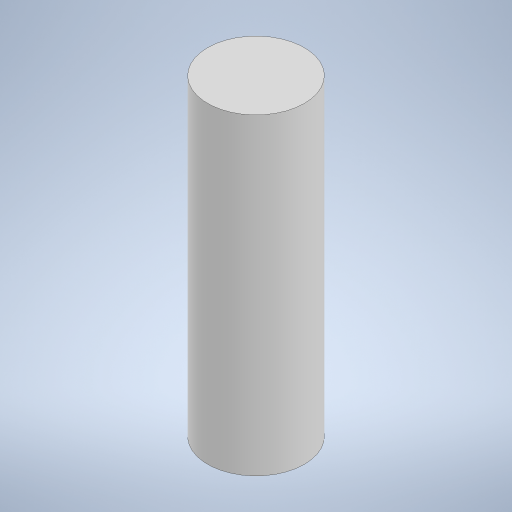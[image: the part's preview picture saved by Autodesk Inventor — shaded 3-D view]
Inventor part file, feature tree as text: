
AUTODESK INVENTOR PART (.ipt)
format: ipt  version: 2023.1 (Build 271208000, 208)  size: 209,408 bytes
history: native  units: mm
features: extrude x1, sketch x1
ambient origin geometry x8: Origin, YZ Plane, XZ Plane, XY Plane, X Axis, Y Axis, Z Axis, Center Point
bodies: Solid1 (feature_tree)
feature tree (2):
  extrude  "Extrusion1"  Depth=9.7mm TaperAngle=0.0deg
  sketch  "Sketch1"  dims[d0=3.0mm d1=9.7mm d2=0.0mm]
